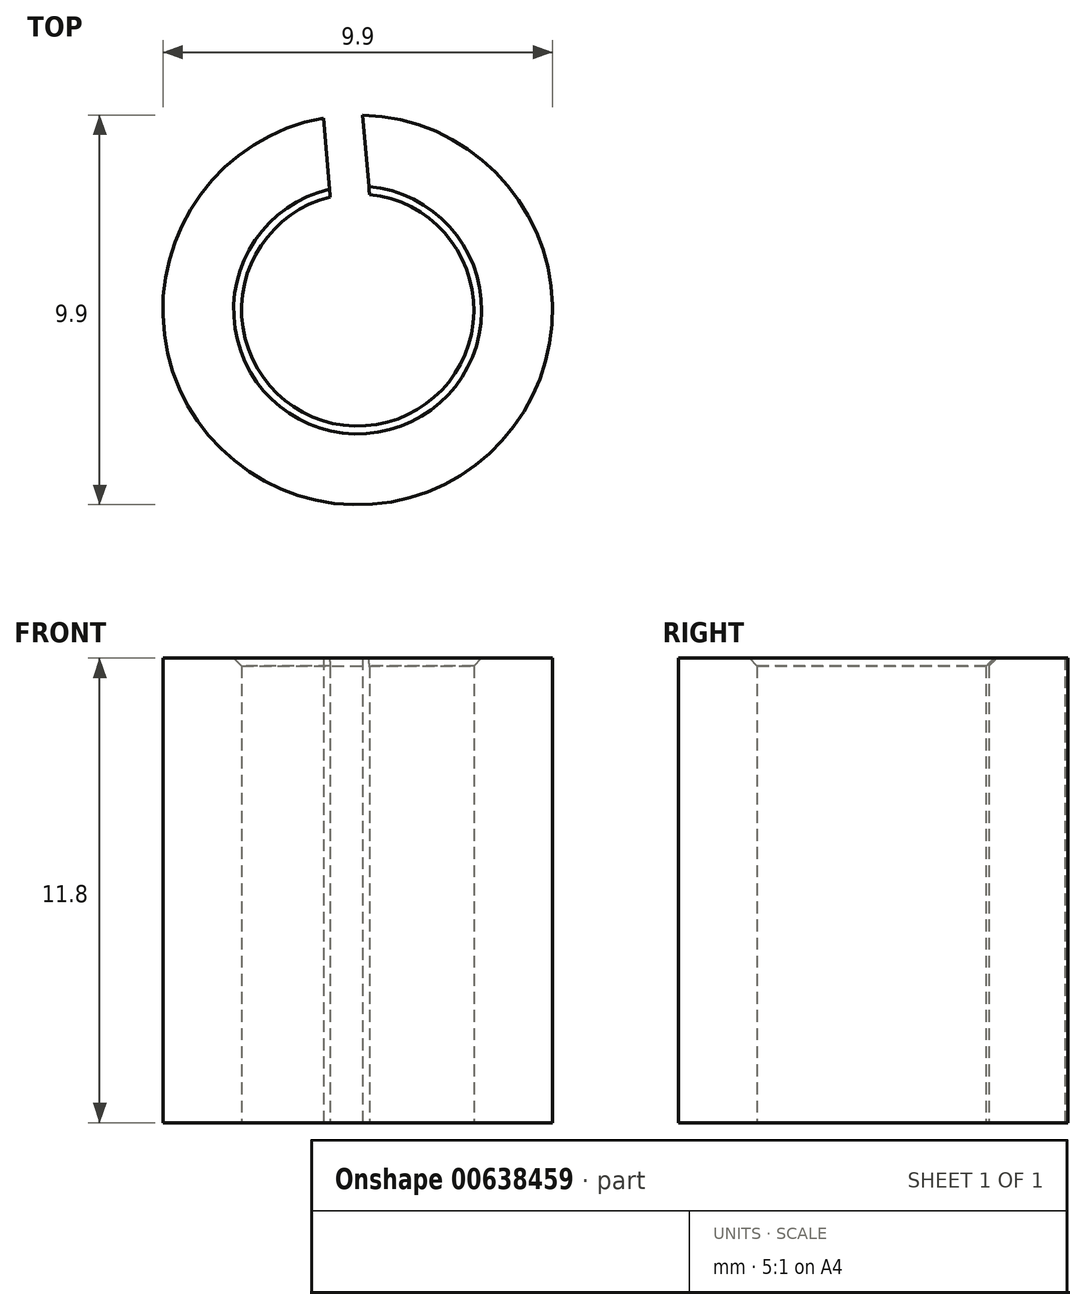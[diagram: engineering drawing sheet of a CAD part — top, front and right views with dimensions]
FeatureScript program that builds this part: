
annotation { "Feature Type Name" : "Feature", "Feature Type Description" : "" }
export const myFeature = defineFeature(function(context is Context, id is Id, definition is map)
    precondition{}
    {
        {
            var Q0;
            Q0=qCreatedBy(makeId("Top.planeOp"),FACE);
            var sketch = newSketch(context, id + "F0", { "sketchPlane" : qUnion([Q0])});
            skArc(sketch, "E0", {"start": v(-0.87, 4.87) * mm, "mid": v(0.37, -4.94) * mm, "end": v(0.13, 4.95) * mm});
            skArc(sketch, "E1", {"start": v(-0.7, 2.87) * mm, "mid": v(0.2, -2.94) * mm, "end": v(0.3, 2.93) * mm});
            skLineSegment(sketch, "E2.left", {"start": v(0.13, 4.95) * mm, "end": v(0.3, 2.93) * mm});
            skLineSegment(sketch, "E2.right", {"start": v(-0.87, 4.87) * mm, "end": v(-0.7, 2.87) * mm});
            skSolve(sketch);
        }
        {
            var Q0;
            Q0 = qSketchRegion(id + "F0", true);
            extrude(context, id + "F1", {"entities" : qUnion([Q0]), "depth" : 11.8 * mm, "offsetDistance" : 25 * mm});
        }
        {
            var Q0;
            Q0=makeQuery(id+"F1.opExtrude","CAP_EDGE",EDGE,{"disambiguationData":[OSD([sQuery(id+"F0.wireOp",EDGE,"E1")])],"isStart":false});
            chamfer(context, id + "F2", {"entities" : qUnion([Q0]), "width" : .2 * mm, "tangentPropagation" : true});
        }
    });
